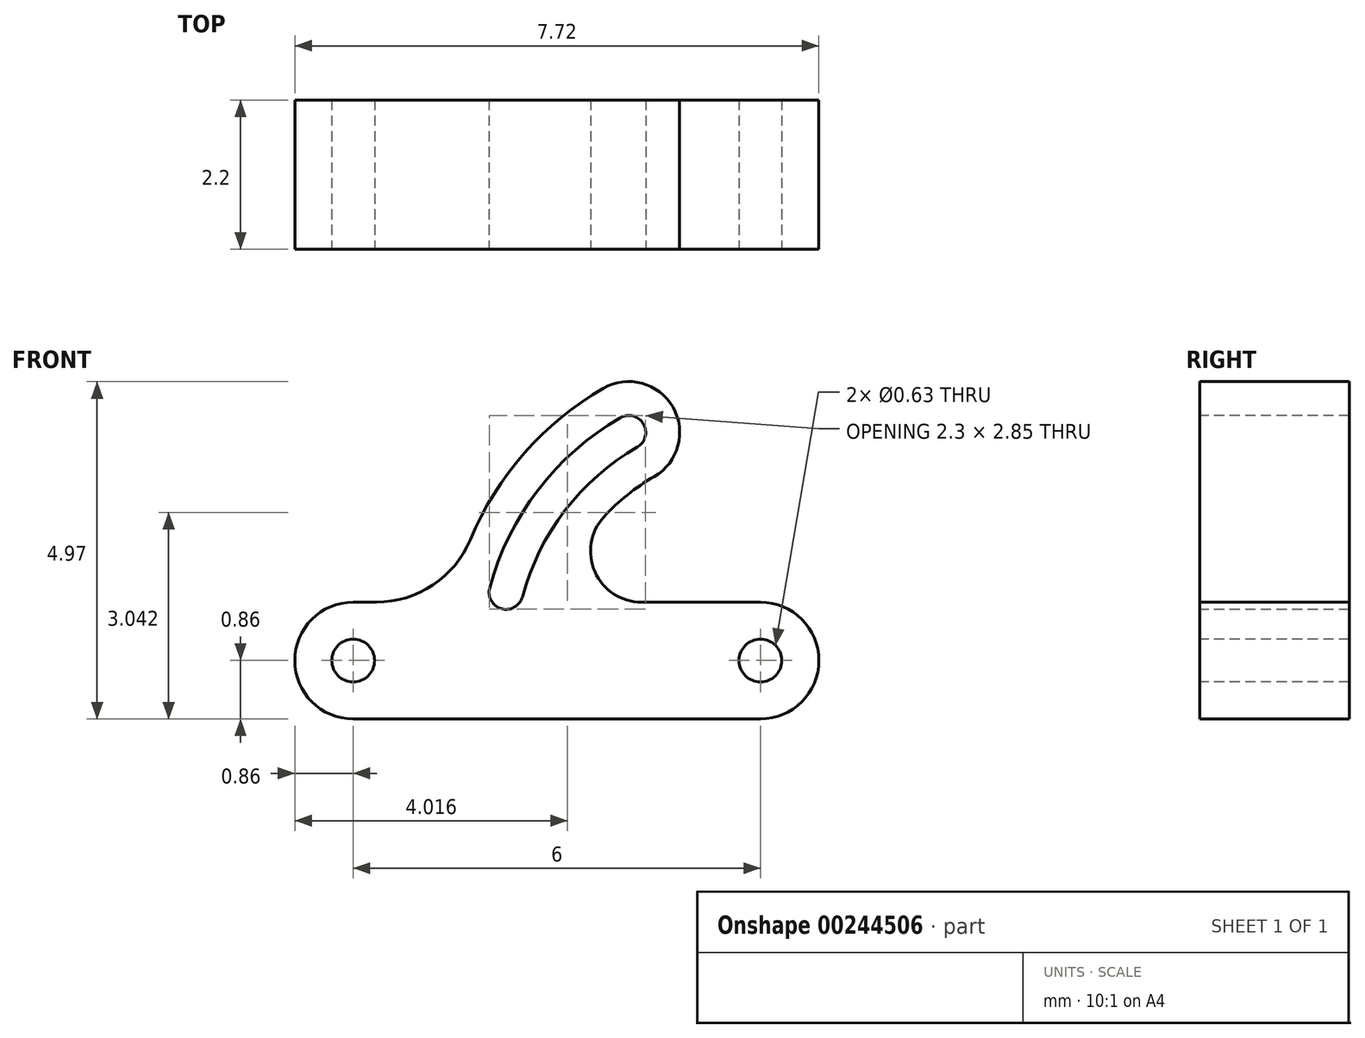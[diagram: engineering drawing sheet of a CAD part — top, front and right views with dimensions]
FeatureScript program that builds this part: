
annotation { "Feature Type Name" : "Feature", "Feature Type Description" : "" }
export const myFeature = defineFeature(function(context is Context, id is Id, definition is map)
    precondition{}
    {
        {
            var Q0;
            Q0=qCreatedBy(makeId("Front.planeOp"),FACE);
            var sketch = newSketch(context, id + "F0", { "sketchPlane" : qUnion([Q0])});
            skCircle(sketch, "E0", {"center": v(0, 0) * mm, "radius": 0.31 * mm});
            skLineSegment(sketch, "E1", {"start": v(0, 0) * mm, "end": v(-6, 0) * mm, "construction": true});
            skLineSegment(sketch, "E2", {"start": v(-3, -1.67) * mm, "end": v(-3, 1.07) * mm, "construction": true});
            skPoint(sketch, "E2.startSnap0", {"position": v(-3, 0) * mm});
            skArc(sketch, "E3", {"start": v(0, -0.86) * mm, "mid": v(0.86, 0) * mm, "end": v(0, 0.86) * mm});
            skLineSegment(sketch, "E4", {"start": v(0, 0.86) * mm, "end": v(-1.75, 0.86) * mm});
            skLineSegment(sketch, "E5", {"start": v(0, -0.86) * mm, "end": v(-3, -0.86) * mm});
            skArc(sketch, "E6.MirrorC", {"start": v(0, 0.86) * mm, "mid": v(0.86, 0) * mm, "end": v(0, -0.86) * mm});
            skCircle(sketch, "E7.MirrorC", {"center": v(-6, 0) * mm, "radius": 0.31 * mm});
            skArc(sketch, "E8.MirrorC", {"start": v(-6, -0.86) * mm, "mid": v(-6.86, 0) * mm, "end": v(-6, 0.86) * mm});
            skLineSegment(sketch, "E9.MirrorCS", {"start": v(-6, 0.86) * mm, "end": v(-5.66, 0.86) * mm});
            skLineSegment(sketch, "E10.MirrorCS", {"start": v(-6, -0.86) * mm, "end": v(-3, -0.86) * mm});
            skArc(sketch, "E11.MirrorC", {"start": v(-6, 0.86) * mm, "mid": v(-6.86, 0) * mm, "end": v(-6, -0.86) * mm});
            skArc(sketch, "E12", {"start": v(0, 3.88) * mm, "mid": v(-3.03, 2.42) * mm, "end": v(-3.78, -0.86) * mm, "construction": true});
            skLineSegment(sketch, "E13", {"start": v(0, 4.7) * mm, "end": v(0, -3.06) * mm, "construction": true});
            skLineSegment(sketch, "E14", {"start": v(0, 0) * mm, "end": v(-2.57, 4.46) * mm, "construction": true});
            skLineSegment(sketch, "E15", {"start": v(0, 0) * mm, "end": v(-7.48, 2) * mm, "construction": true});
            skArc(sketch, "E16", {"start": v(-1.82, 3.14) * mm, "mid": v(-1.72, 3.49) * mm, "end": v(-2.06, 3.58) * mm});
            skArc(sketch, "E17", {"start": v(-3.99, 1.07) * mm, "mid": v(-3.81, 0.76) * mm, "end": v(-3.5, 0.94) * mm});
            skArc(sketch, "E18", {"start": v(-1.82, 3.14) * mm, "mid": v(-2.88, 2.2) * mm, "end": v(-3.5, 0.94) * mm});
            skArc(sketch, "E19", {"start": v(-2.06, 3.58) * mm, "mid": v(-3.28, 2.51) * mm, "end": v(-3.99, 1.07) * mm});
            skArc(sketch, "E20", {"start": v(-1.57, 2.71) * mm, "mid": v(-1.3, 3.74) * mm, "end": v(-2.32, 4) * mm});
            skArc(sketch, "E21", {"start": v(-1.57, 2.71) * mm, "mid": v(-1.96, 2.44) * mm, "end": v(-2.3, 2.12) * mm});
            skArc(sketch, "E22", {"start": v(-2.32, 4) * mm, "mid": v(-3.48, 3.06) * mm, "end": v(-4.27, 1.78) * mm});
            skArc(sketch, "E23.trimOffspring", {"start": v(-3, -0.86) * mm, "mid": v(-3, -0.88) * mm, "end": v(-3, -0.9) * mm});
            skArc(sketch, "E24.filletArc", {"start": v(-5.66, 0.86) * mm, "mid": v(-4.83, 1.11) * mm, "end": v(-4.27, 1.78) * mm});
            skArc(sketch, "E25.filletArc", {"start": v(-2.3, 2.12) * mm, "mid": v(-2.44, 1.3) * mm, "end": v(-1.75, 0.86) * mm});
            skSolve(sketch);
        }
        {
            var Q0;
            Q0=makeQuery(id+"F0.imprint","IMPRINT",FACE,{"disambiguationData":[TD([[makeQuery(id+"F0.imprint","IMPRINT",EDGE,{"derivedFrom":sQuery(id+"F0.wireOp",EDGE,"E4")}),1.0]])]});
            extrude(context, id + "F1", {"entities" : qUnion([Q0]), "oppositeDirection" : true, "depth" : 2.2 * mm});
        }
    });
